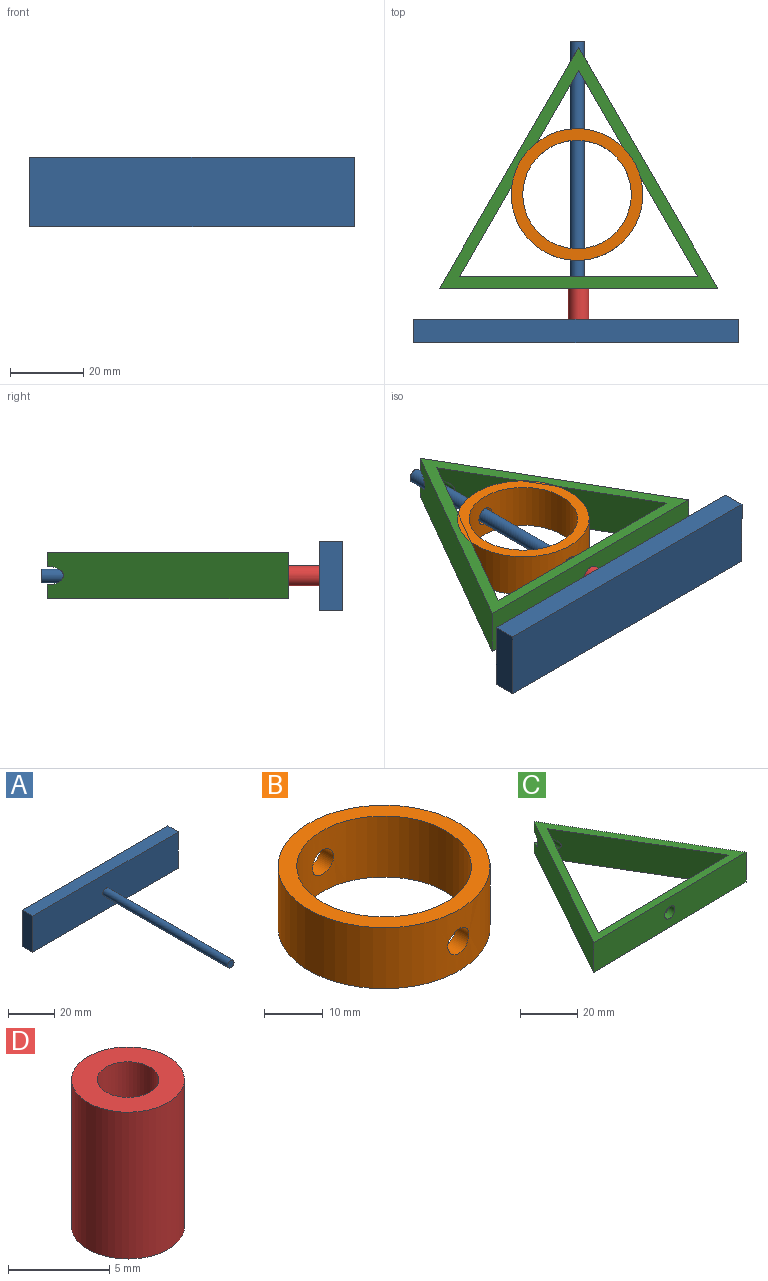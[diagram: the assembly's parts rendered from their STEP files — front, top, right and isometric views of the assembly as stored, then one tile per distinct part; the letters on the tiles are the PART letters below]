
ASSEMBLY  parts=4 mates=4
PART A: 8 faces, bbox 88.9x82.6x19.1 mm
  f0: cylinder r=1.91mm len=76.2mm, axis (0,1,0), area 912.1mm2, adj f1,f7
  f1: plane 3.81x3.81mm, normal (0,-1,0), area 11.4mm2, adj f0
  f2: plane 88.9x6.35mm, normal (0,0,1), area 564.5mm2, adj f3,f5,f6,f7
  f3: plane 19.05x6.35mm, normal (-1,0,0), area 121mm2, adj f2,f4,f6,f7
  f4: plane 88.9x6.35mm, normal (0,0,-1), area 564.5mm2, adj f3,f5,f6,f7
  f5: plane 19.05x6.35mm, normal (1,0,0), area 121mm2, adj f2,f4,f6,f7
  f6: plane 88.9x19.05mm, normal (0,1,0), area 1693.5mm2, adj f2,f3,f4,f5
  f7: plane 88.9x19.05mm, normal (0,-1,0), area 1682.1mm2, adj f0,f2,f3,f4,f5
PART B: 6 faces, bbox 36.1x36.1x12.7 mm
  f0: cylinder r=14.86mm len=29.72mm, axis (0,0,-1), area 1144.8mm2, adj f2,f3,f4,f5
  f1: cylinder r=18.03mm len=36.07mm, axis (0,0,-1), area 1398.2mm2, adj f2,f3,f4,f5
  f2: plane 36.07x36.07mm, normal (0,0,1), area 328.1mm2, adj f0,f1
  f3: plane 36.07x36.07mm, normal (0,0,-1), area 328.1mm2, adj f0,f1
  f4: cylinder r=2.54mm len=5.08mm, axis (0,-1,0), area 51mm2, adj f0,f1
  f5: cylinder r=2.54mm len=5.08mm, axis (0,1,0), area 51mm2, adj f0,f1
PART C: 10 faces, bbox 76.2x66.6x12.7 mm
  f0: plane 55.98x33.42mm, normal (-0.86,-0.51,0), area 807.8mm2, adj f1,f5,f6,f7,f8
  f1: plane 65.19x12.7mm, normal (-0.01,1,0), area 807.8mm2, adj f0,f5,f6,f7,f9
  f2: plane 76.19x12.7mm, normal (0.01,-1,0), area 947.5mm2, adj f3,f4,f6,f7,f9
  f3: plane 65.43x39.06mm, normal (0.86,0.51,0), area 947.5mm2, adj f2,f4,f6,f7,f8
  f4: plane 66.54x37.13mm, normal (-0.87,0.49,0), area 947.5mm2, adj f2,f3,f6,f7,f8
  f5: plane 56.94x31.77mm, normal (0.87,-0.49,0), area 807.8mm2, adj f0,f1,f6,f7,f8
  f6: plane 76.19x66.54mm, normal (0,0,1), area 673.4mm2, adj f0,f1,f2,f3,f4,f5
  f7: plane 76.19x66.54mm, normal (0,0,-1), area 673.4mm2, adj f0,f1,f2,f3,f4,f5
  f8: cylinder r=2.54mm len=10.84mm, axis (0.01,-1,0), area 101.3mm2, adj f0,f3,f4,f5
  f9: cylinder r=2.54mm len=5.13mm, axis (0.01,-1,0), area 50.7mm2, adj f1,f2
PART D: 4 faces, bbox 5.6x5.6x8.9 mm
  f0: cylinder r=1.52mm len=8.89mm, axis (0,0,1), area 85.1mm2, adj f2,f3
  f1: cylinder r=2.79mm len=8.89mm, axis (0,0,1), area 156.1mm2, adj f2,f3
  f2: plane 5.59x5.59mm, normal (0,0,-1), area 17.2mm2, adj f0,f1
  f3: plane 5.59x5.59mm, normal (0,0,1), area 17.2mm2, adj f0,f1
PLACE A rot(axis=(1,0,0),180deg) t=(-1.22,-43.32,2.91)mm
PLACE B t=(-1.22,-9.11,-3.28)mm fixed
PLACE C rot(axis=(0,0,-1),0.8deg) t=(-0.77,-1.76,-3.36)mm
PLACE D rot(axis=(-1,0,0),90deg) t=(-0.77,-34.75,2.99)mm
MATE parallel A.f4 <-> B.f1  axis (0,0,1) through (-1.5,-46.5,12.43)mm
MATE fastened C.f8 <-> D.f1  axis (0,-1,0) through (-0.77,-34.75,2.99)mm
MATE fastened D.f1 <-> D.f1  axis (0,1,0) through (-0.77,-43.64,2.99)mm
MATE cylindrical A.f0 <-> B.f4  axis (0,1,0) through (-1.22,32.88,2.91)mm
